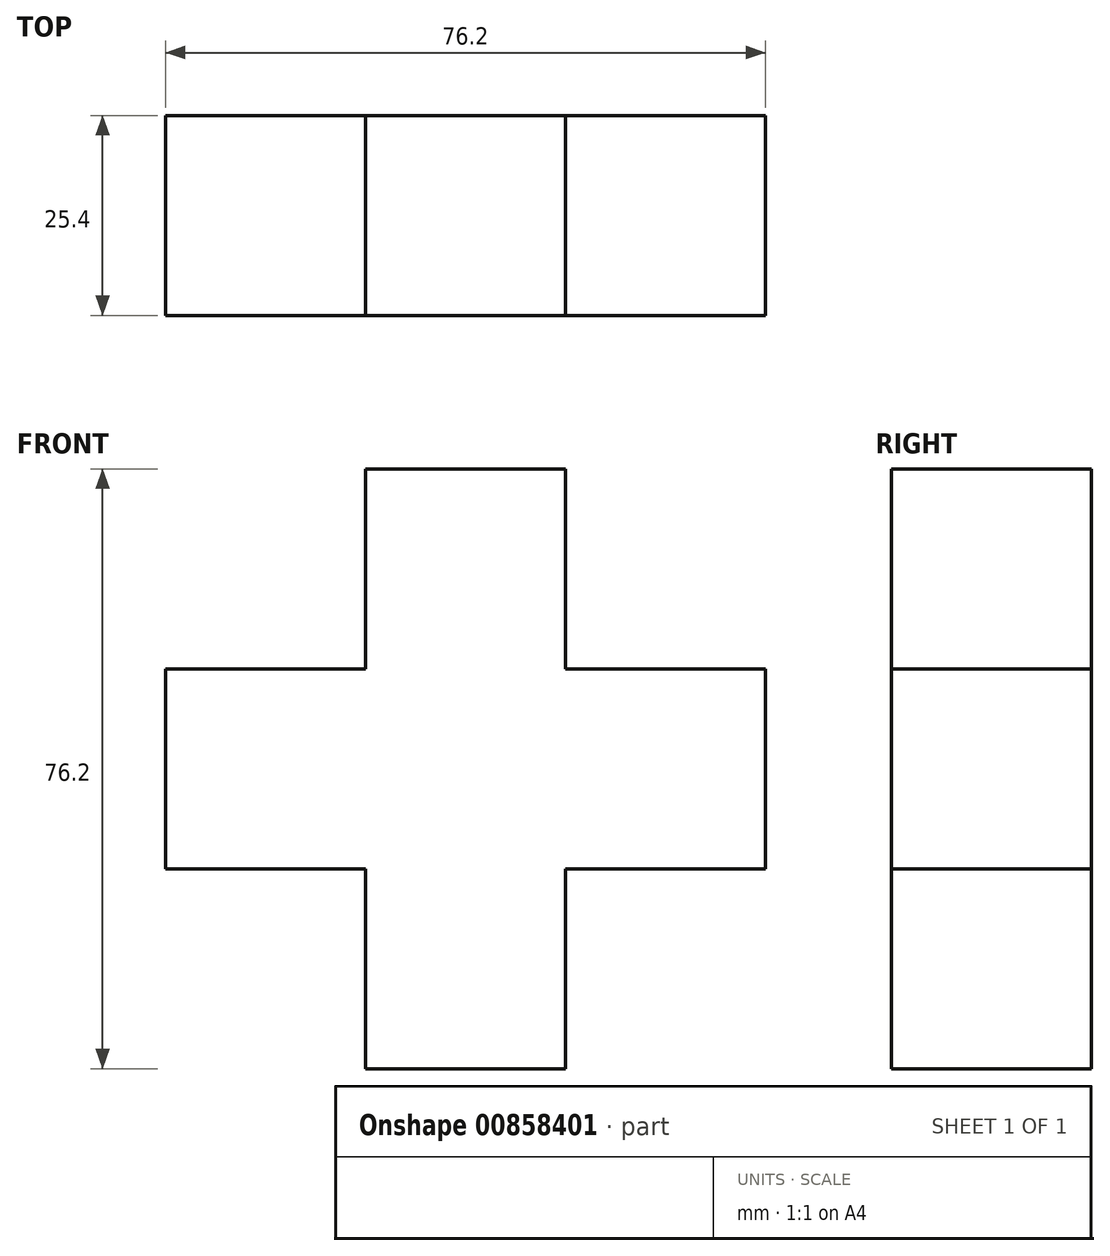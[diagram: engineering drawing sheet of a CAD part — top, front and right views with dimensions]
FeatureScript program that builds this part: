
annotation { "Feature Type Name" : "Feature", "Feature Type Description" : "" }
export const myFeature = defineFeature(function(context is Context, id is Id, definition is map)
    precondition{}
    {
        {
            var Q0;
            Q0=qCreatedBy(makeId("Front.planeOp"),FACE);
            var sketch = newSketch(context, id + "F0", { "sketchPlane" : qUnion([Q0])});
            skLineSegment(sketch, "E0", {"start": v(20.46, 0) * mm, "end": v(20.46, 25.4) * mm});
            skLineSegment(sketch, "E1", {"start": v(20.46, 25.4) * mm, "end": v(-4.94, 25.4) * mm});
            skLineSegment(sketch, "E2", {"start": v(-4.94, 25.4) * mm, "end": v(-4.94, 0) * mm});
            skLineSegment(sketch, "E3", {"start": v(-4.94, 0) * mm, "end": v(-30.34, 0) * mm});
            skLineSegment(sketch, "E4", {"start": v(-30.34, 0) * mm, "end": v(-30.34, -25.4) * mm});
            skLineSegment(sketch, "E5", {"start": v(-30.34, -25.4) * mm, "end": v(-4.94, -25.4) * mm});
            skLineSegment(sketch, "E6", {"start": v(-4.94, -25.4) * mm, "end": v(-4.94, -50.8) * mm});
            skLineSegment(sketch, "E7", {"start": v(-4.94, -50.8) * mm, "end": v(20.46, -50.8) * mm});
            skLineSegment(sketch, "E8", {"start": v(20.46, -50.8) * mm, "end": v(20.46, -25.4) * mm});
            skLineSegment(sketch, "E9", {"start": v(20.46, -25.4) * mm, "end": v(45.86, -25.4) * mm});
            skLineSegment(sketch, "E10", {"start": v(45.86, -25.4) * mm, "end": v(45.86, 0) * mm});
            skLineSegment(sketch, "E11", {"start": v(45.86, 0) * mm, "end": v(20.46, 0) * mm});
            skLineSegment(sketch, "E12", {"start": v(20.46, 0) * mm, "end": v(20.46, 0) * mm});
            skSolve(sketch);
        }
        {
            var Q0;
            Q0=makeQuery(id+"F0.imprint","IMPRINT",FACE,{"disambiguationData":[TD([[makeQuery(id+"F0.imprint","IMPRINT",EDGE,{"derivedFrom":sQuery(id+"F0.wireOp",EDGE,"E0")}),1.0]])]});
            extrude(context, id + "F1", {"entities" : qUnion([Q0]), "depth" : 25.4 * mm, "offsetDistance" : 25.4 * mm});
        }
    });
